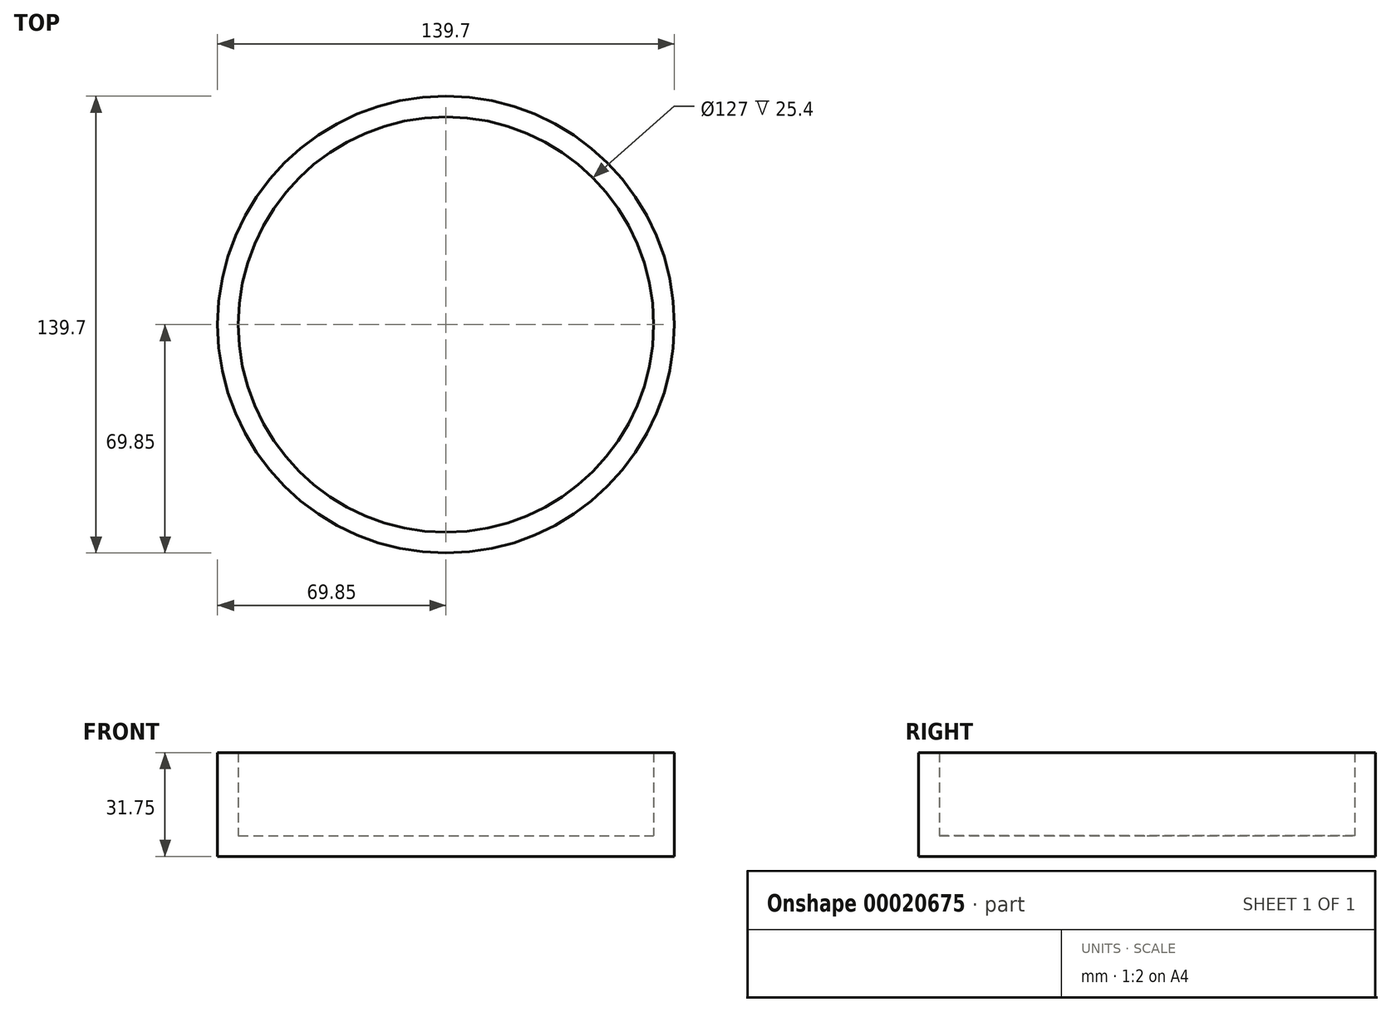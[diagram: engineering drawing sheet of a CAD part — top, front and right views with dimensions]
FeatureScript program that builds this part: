
annotation { "Feature Type Name" : "Feature", "Feature Type Description" : "" }
export const myFeature = defineFeature(function(context is Context, id is Id, definition is map)
    precondition{}
    {
        {
            var Q0;
            Q0=qCreatedBy(makeId("Front.planeOp"),FACE);
            var sketch = newSketch(context, id + "F0", { "sketchPlane" : qUnion([Q0])});
            skLineSegment(sketch, "E0", {"start": v(0, 0) * mm, "end": v(63.5, 0) * mm});
            skLineSegment(sketch, "E1", {"start": v(63.5, 0) * mm, "end": v(63.5, 25.4) * mm});
            skLineSegment(sketch, "E2", {"start": v(63.5, 25.4) * mm, "end": v(69.85, 25.4) * mm});
            skLineSegment(sketch, "E3", {"start": v(69.85, 25.4) * mm, "end": v(69.85, -6.35) * mm});
            skLineSegment(sketch, "E4", {"start": v(69.85, -6.35) * mm, "end": v(0, -6.35) * mm});
            skLineSegment(sketch, "E5", {"start": v(0, -6.35) * mm, "end": v(0, 0) * mm});
            skLineSegment(sketch, "E6", {"start": v(0, 0) * mm, "end": v(0, 25.4) * mm, "construction": true});
            skSolve(sketch);
        }
        {
            var Q0;
            Q0=makeQuery(id+"F0.imprint","IMPRINT",FACE,{"disambiguationData":[TD([[makeQuery(id+"F0.imprint","IMPRINT",EDGE,{"derivedFrom":sQuery(id+"F0.wireOp",EDGE,"E0")}),-1.0]])]});
            var Q1;
            Q1=sQuery(id+"F0.wireOp",EDGE,"E6");
            revolve(context, id + "F1", {"entities" : qUnion([Q0]), "axis" : qUnion([Q1]), "revolveType" : RevolveType.FULL});
        }
    });
